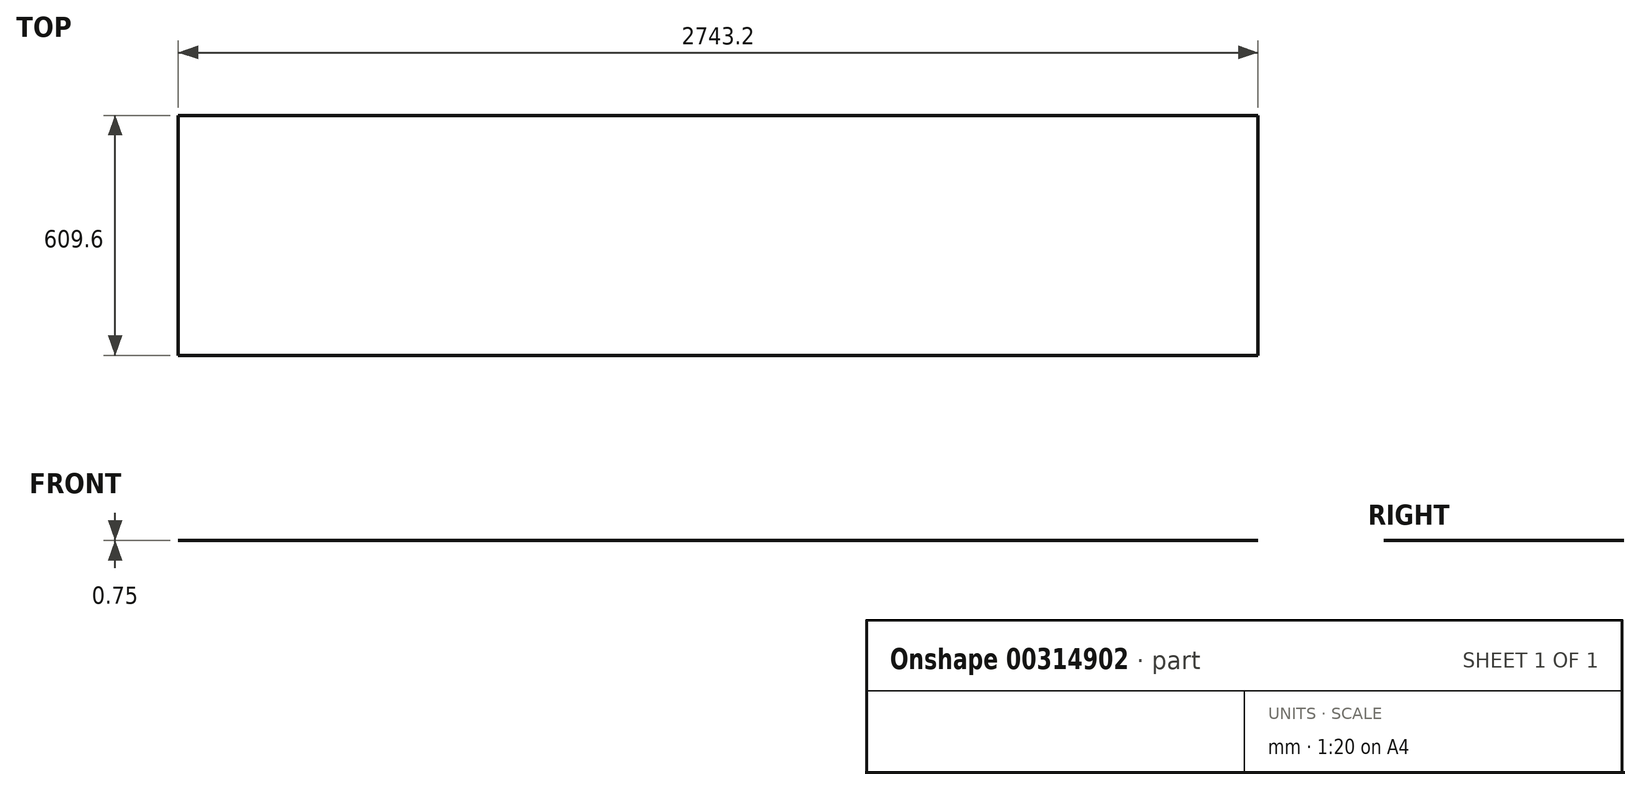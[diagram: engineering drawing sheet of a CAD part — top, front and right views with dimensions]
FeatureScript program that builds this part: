
annotation { "Feature Type Name" : "Feature", "Feature Type Description" : "" }
export const myFeature = defineFeature(function(context is Context, id is Id, definition is map)
    precondition{}
    {
        {
            assignVariable(context, id + "F0", {"name" : "Thickness", "anyValue" : .75});
        }
        {
            var Q0;
            Q0=qCreatedBy(makeId("Top.planeOp"),FACE);
            var sketch = newSketch(context, id + "F1", { "sketchPlane" : qUnion([Q0])});
            skLineSegment(sketch, "E0.bottom", {"start": v(-1371.6, 304.8) * mm, "end": v(1371.6, 304.8) * mm});
            skLineSegment(sketch, "E0.top", {"start": v(-1371.6, -304.8) * mm, "end": v(1371.6, -304.8) * mm});
            skLineSegment(sketch, "E0.left", {"start": v(-1371.6, 304.8) * mm, "end": v(-1371.6, -304.8) * mm});
            skLineSegment(sketch, "E0.right", {"start": v(1371.6, 304.8) * mm, "end": v(1371.6, -304.8) * mm});
            skPoint(sketch, "E0.middle", {"position": v(0, 0) * mm});
            skSolve(sketch);
        }
        {
            var Q0;
            Q0=makeQuery(id+"F1.imprint","IMPRINT",FACE,{"disambiguationData":[TD([[makeQuery(id+"F1.imprint","IMPRINT",EDGE,{"derivedFrom":sQuery(id+"F1.wireOp",EDGE,"E0.bottom")}),-1.0]])]});
            extrude(context, id + "F2", {"entities" : qUnion([Q0]), "oppositeDirection" : true, "depth" : (getVariable(context, 'Thickness')) * mm});
        }
    });
